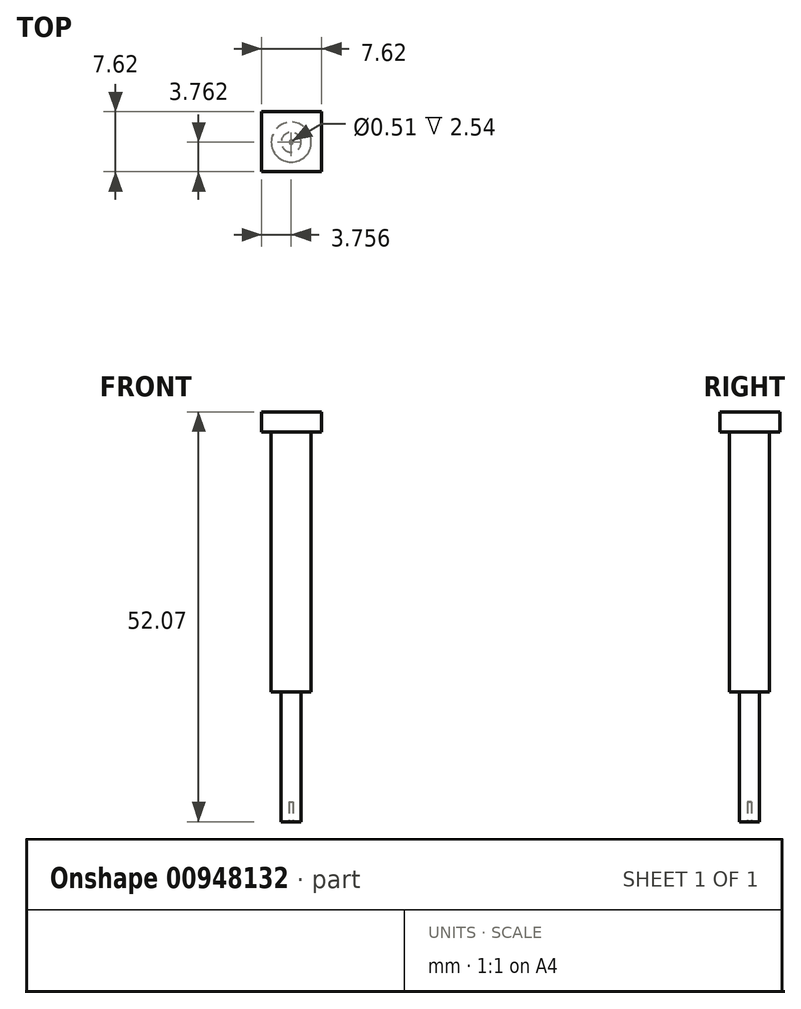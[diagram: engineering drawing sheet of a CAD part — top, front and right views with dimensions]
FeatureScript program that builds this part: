
annotation { "Feature Type Name" : "Feature", "Feature Type Description" : "" }
export const myFeature = defineFeature(function(context is Context, id is Id, definition is map)
    precondition{}
    {
        {
            var Q0;
            Q0=qCreatedBy(makeId("Top.planeOp"),FACE);
            var sketch = newSketch(context, id + "F0", { "sketchPlane" : qUnion([Q0])});
            skLineSegment(sketch, "E0.bottom", {"start": v(-42.6, -18.03) * mm, "end": v(-34.99, -18.03) * mm});
            skLineSegment(sketch, "E0.top", {"start": v(-42.6, -25.65) * mm, "end": v(-34.99, -25.65) * mm});
            skLineSegment(sketch, "E0.left", {"start": v(-42.6, -18.03) * mm, "end": v(-42.6, -25.65) * mm});
            skLineSegment(sketch, "E0.right", {"start": v(-34.99, -18.03) * mm, "end": v(-34.99, -25.65) * mm});
            skSolve(sketch);
        }
        {
            var Q0;
            Q0=qSketchRegion(id+"F0",true);
            extrude(context, id + "F1", {"entities" : qUnion([Q0]), "depth" : 2.54 * mm, "offsetDistance" : 25.4 * mm});
        }
        {
            var Q0;
            Q0=makeQuery(id+"F1.opExtrude","CAP_FACE",FACE,{"disambiguationData":[OSD([sQuery(id+"F0.wireOp",EDGE,"E0.bottom"),sQuery(id+"F0.wireOp",EDGE,"E0.top"),sQuery(id+"F0.wireOp",EDGE,"E0.left"),sQuery(id+"F0.wireOp",EDGE,"E0.right")])],"isStart":true});
            var sketch = newSketch(context, id + "F2", { "sketchPlane" : qUnion([Q0])});
            skCircle(sketch, "E1", {"center": v(-38.85, 21.89) * mm, "radius": 2.54 * mm});
            skCircle(sketch, "E2", {"center": v(-38.85, 21.89) * mm, "radius": 1.27 * mm});
            skSolve(sketch);
        }
        {
            var Q0;
            Q0=makeQuery(id+"F2.imprint","IMPRINT",FACE,{"disambiguationData":[TD([[makeQuery(id+"F2.imprint","IMPRINT",EDGE,{"derivedFrom":sQuery(id+"F2.wireOp",EDGE,"E2")}),1.0]])]});
            extrude(context, id + "F3", {"entities" : qUnion([Q0]), "operationType" : NewBodyOperationType.ADD, "depth" : 49.53 * mm, "offsetDistance" : 25.4 * mm});
        }
        {
            var Q0;
            Q0=makeQuery(id+"F3.opExtrude","CAP_FACE",FACE,{"disambiguationData":[OSD([sQuery(id+"F2.wireOp",EDGE,"E2")])],"isStart":false});
            var sketch = newSketch(context, id + "F4", { "sketchPlane" : qUnion([Q0])});
            skCircle(sketch, "E3", {"center": v(-38.85, 21.89) * mm, "radius": 0.25 * mm});
            skSolve(sketch);
        }
        {
            var Q0;
            Q0=qSketchRegion(id+"F4",true);
            extrude(context, id + "F5", {"entities" : qUnion([Q0]), "operationType" : NewBodyOperationType.REMOVE, "oppositeDirection" : true, "depth" : 2.54 * mm, "offsetDistance" : 25.4 * mm});
        }
        {
            var Q0;
            Q0=qSketchRegion(id+"F2",true);
            extrude(context, id + "F6", {"entities" : qUnion([Q0]), "operationType" : NewBodyOperationType.ADD, "depth" : 33.02 * mm, "offsetDistance" : 25.4 * mm});
        }
    });
